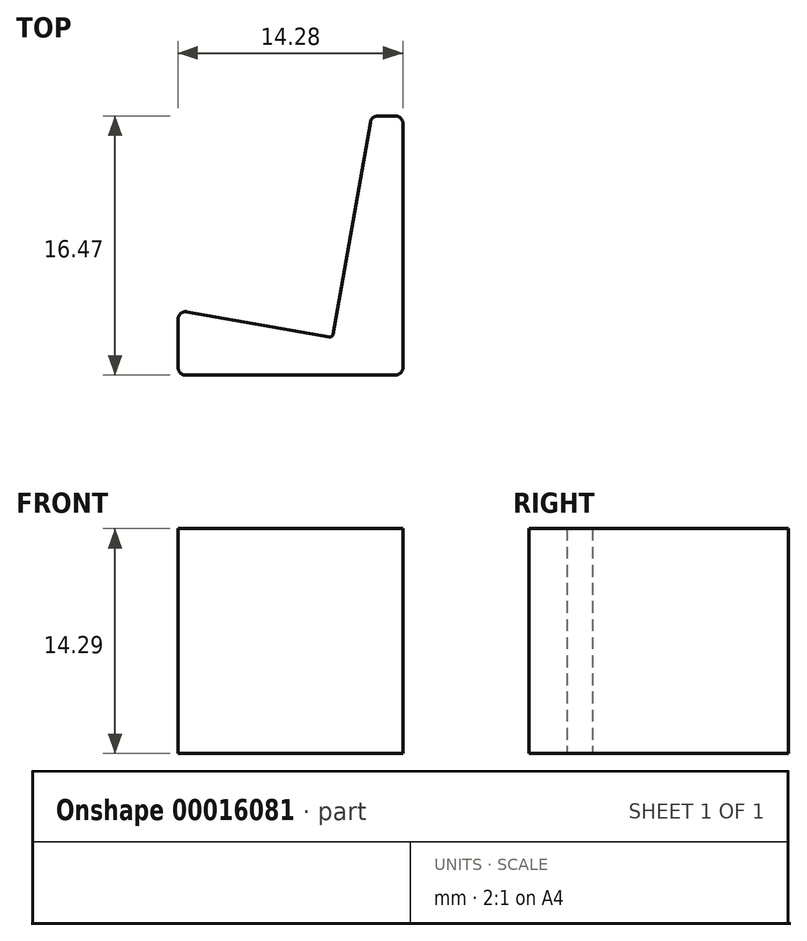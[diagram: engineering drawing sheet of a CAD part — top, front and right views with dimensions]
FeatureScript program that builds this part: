
annotation { "Feature Type Name" : "Feature", "Feature Type Description" : "" }
export const myFeature = defineFeature(function(context is Context, id is Id, definition is map)
    precondition{}
    {
        {
            var Q0;
            Q0=qCreatedBy(makeId("Top.planeOp"),FACE);
            var sketch = newSketch(context, id + "F0", { "sketchPlane" : qUnion([Q0])});
            skLineSegment(sketch, "E0", {"start": v(2.47, 2.43) * mm, "end": v(-6.56, 4.03) * mm});
            skLineSegment(sketch, "E1", {"start": v(-7.14, 3.53) * mm, "end": v(-7.14, 0) * mm});
            skLineSegment(sketch, "E2", {"start": v(-7.14, 0) * mm, "end": v(7.14, 0) * mm});
            skLineSegment(sketch, "E3", {"start": v(7.14, 0) * mm, "end": v(7.14, 15.97) * mm});
            skLineSegment(sketch, "E4", {"start": v(2.7, 2.6) * mm, "end": v(5.07, 16.06) * mm});
            skLineSegment(sketch, "E5", {"start": v(5.56, 16.47) * mm, "end": v(6.64, 16.47) * mm});
            skPoint(sketch, "E6.visualSharp", {"position": v(5.14, 16.47) * mm});
            skArc(sketch, "E6.filletArc", {"start": v(5.56, 16.47) * mm, "mid": v(5.24, 16.35) * mm, "end": v(5.07, 16.06) * mm});
            skPoint(sketch, "E7.visualSharp", {"position": v(7.14, 16.47) * mm});
            skArc(sketch, "E7.filletArc", {"start": v(7.14, 15.97) * mm, "mid": v(7, 16.32) * mm, "end": v(6.64, 16.47) * mm});
            skPoint(sketch, "E8.visualSharp", {"position": v(-7.14, 4.13) * mm});
            skArc(sketch, "E8.filletArc", {"start": v(-6.56, 4.03) * mm, "mid": v(-6.97, 3.92) * mm, "end": v(-7.14, 3.53) * mm});
            skPoint(sketch, "E9.visualSharp", {"position": v(2.66, 2.4) * mm});
            skArc(sketch, "E9.filletArc", {"start": v(2.47, 2.43) * mm, "mid": v(2.62, 2.47) * mm, "end": v(2.7, 2.6) * mm});
            skArc(sketch, "E10.0", {"start": v(2.33, 1.65) * mm, "mid": v(3.07, 1.81) * mm, "end": v(3.49, 2.46) * mm});
            skLineSegment(sketch, "E10.1", {"start": v(2.33, 1.65) * mm, "end": v(-6.34, 3.18) * mm});
            skLineSegment(sketch, "E10.3", {"start": v(-6.34, 3.18) * mm, "end": v(-6.34, 0.8) * mm});
            skLineSegment(sketch, "E10.4", {"start": v(-6.34, 0.8) * mm, "end": v(6.34, 0.8) * mm});
            skLineSegment(sketch, "E10.5", {"start": v(3.49, 2.46) * mm, "end": v(5.82, 15.67) * mm});
            skLineSegment(sketch, "E10.6", {"start": v(6.34, 0.8) * mm, "end": v(6.34, 15.67) * mm});
            skLineSegment(sketch, "E10.8", {"start": v(5.82, 15.67) * mm, "end": v(6.34, 15.67) * mm});
            skSolve(sketch);
        }
        {
            var Q0;
            Q0=qSketchRegion(id+"F0",true);
            var Q1;
            Q1=makeQuery(id+"F0.imprint","IMPRINT",FACE,{"disambiguationData":[TD([[makeQuery(id+"F0.imprint","IMPRINT",EDGE,{"derivedFrom":sQuery(id+"F0.wireOp",EDGE,"E10.0")}),-1.0]])]});
            extrude(context, id + "F1", {"entities" : qUnion([Q0, Q1]), "depth" : 14.29 * mm});
        }
        {
            var Q0;
            Q0=makeQuery(id+"F1.opExtrude","SWEPT_EDGE",EDGE,{"disambiguationData":[OSD([sQuery(id+"F0.wireOp",EDGE,"E4"),sQuery(id+"F0.wireOp",EDGE,"E5")])]});
            var Q1;
            Q1=makeQuery(id+"F1.opExtrude","SWEPT_EDGE",EDGE,{"disambiguationData":[OSD([sQuery(id+"F0.wireOp",EDGE,"E0"),sQuery(id+"F0.wireOp",EDGE,"E1")])]});
            var Q2;
            Q2=makeQuery(id+"F1.opExtrude","SWEPT_EDGE",EDGE,{"disambiguationData":[OSD([sQuery(id+"F0.wireOp",EDGE,"E3"),sQuery(id+"F0.wireOp",EDGE,"E5")])]});
            fillet(context, id + "F2", {"entities" : qUnion([Q0, Q1, Q2]), "radius" : .5 * mm, "tangentPropagation" : true, "allowEdgeOverflow" : false});
        }
    });
